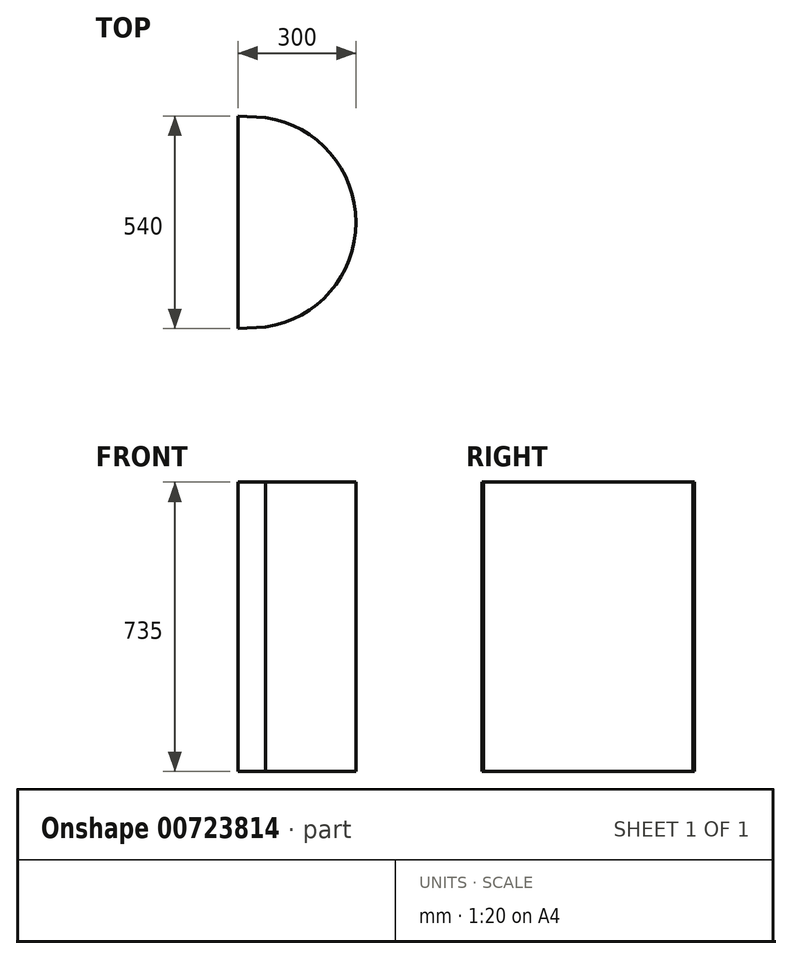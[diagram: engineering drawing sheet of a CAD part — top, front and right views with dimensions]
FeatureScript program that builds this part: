
annotation { "Feature Type Name" : "Feature", "Feature Type Description" : "" }
export const myFeature = defineFeature(function(context is Context, id is Id, definition is map)
    precondition{}
    {
        {
            var Q0;
            Q0=qCreatedBy(makeId("Top.planeOp"),FACE);
            var sketch = newSketch(context, id + "F0", { "sketchPlane" : qUnion([Q0])});
            skLineSegment(sketch, "E0.left", {"start": v(-428.36, 270) * mm, "end": v(-428.36, -270) * mm});
            skArc(sketch, "E1", {"start": v(-358.47, -266.17) * mm, "mid": v(-128.36, 0) * mm, "end": v(-358.47, 266.17) * mm});
            skLineSegment(sketch, "E2", {"start": v(-358.47, -266.17) * mm, "end": v(-428.36, -270) * mm});
            skLineSegment(sketch, "E3", {"start": v(-358.47, 266.17) * mm, "end": v(-428.36, 270) * mm});
            skPoint(sketch, "E4.start.orphan", {"position": v(-428.36, 0) * mm});
            skSolve(sketch);
        }
        {
            var Q0;
            Q0=makeQuery(id+"F0.imprint","IMPRINT",FACE,{"disambiguationData":[TD([[makeQuery(id+"F0.imprint","IMPRINT",EDGE,{"derivedFrom":sQuery(id+"F0.wireOp",EDGE,"E0.left")}),1.0]])]});
            var Q1;
            Q1=sQuery(id+"F0.wireOp",EDGE,"E0.left");
            var Q2;
            Q2=sQuery(id+"F0.wireOp",EDGE,"E1");
            var Q3;
            Q3=sQuery(id+"F0.wireOp",EDGE,"E3");
            var Q4;
            Q4=sQuery(id+"F0.wireOp",EDGE,"E2");
            extrude(context, id + "F1", {"entities" : qUnion([Q0]), "bodyType" : ToolBodyType.SURFACE, "surfaceEntities" : qUnion([Q1, Q2, Q3, Q4]), "depth" : 735 * mm, "offsetDistance" : 25 * mm});
        }
    });
